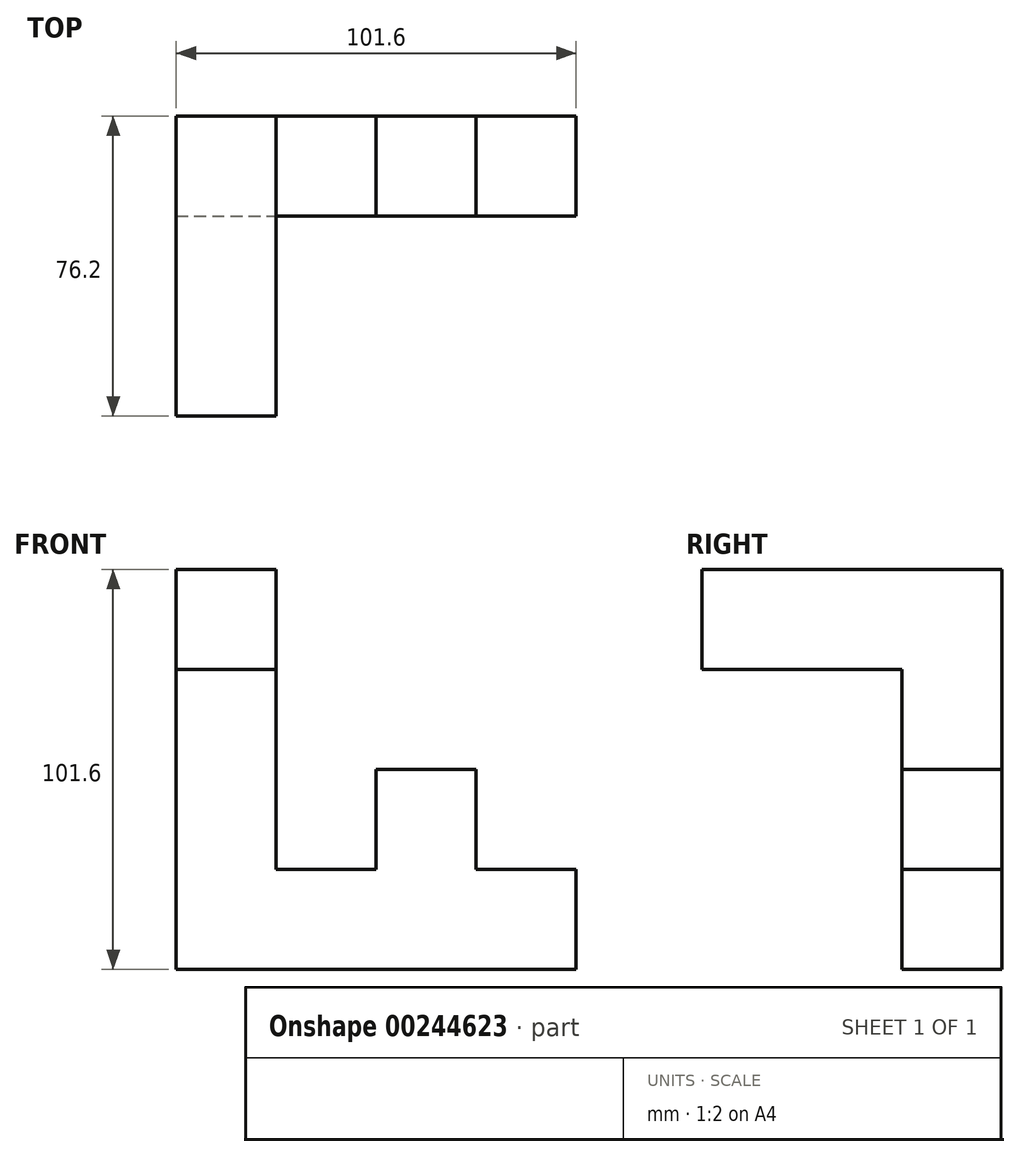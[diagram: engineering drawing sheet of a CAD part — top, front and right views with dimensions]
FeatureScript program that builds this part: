
annotation { "Feature Type Name" : "Feature", "Feature Type Description" : "" }
export const myFeature = defineFeature(function(context is Context, id is Id, definition is map)
    precondition{}
    {
        {
            var Q0;
            Q0=qCreatedBy(makeId("Top.planeOp"),FACE);
            var sketch = newSketch(context, id + "F0", { "sketchPlane" : qUnion([Q0])});
            skLineSegment(sketch, "E0.bottom", {"start": v(0, 0) * mm, "end": v(101.6, 0) * mm});
            skLineSegment(sketch, "E0.top", {"start": v(0, 25.4) * mm, "end": v(101.6, 25.4) * mm});
            skLineSegment(sketch, "E0.left", {"start": v(0, 0) * mm, "end": v(0, 25.4) * mm});
            skLineSegment(sketch, "E0.right", {"start": v(101.6, 0) * mm, "end": v(101.6, 25.4) * mm});
            skLineSegment(sketch, "E1", {"start": v(25.4, 25.4) * mm, "end": v(25.4, 0) * mm});
            skLineSegment(sketch, "E2", {"start": v(50.8, 25.4) * mm, "end": v(50.8, 0) * mm});
            skLineSegment(sketch, "E3", {"start": v(76.2, 25.4) * mm, "end": v(76.2, 0) * mm});
            skSolve(sketch);
        }
        {
            var Q0;
            {var subQ2=sQuery(id+"F0.wireOp",EDGE,"E1");Q0=makeQuery(id+"F0.imprint","IMPRINT",FACE,{"disambiguationData":[TD([[makeQuery(id+"F0.imprint","IMPRINT",EDGE,{"derivedFrom":subQ2}),1.0]])]});}
            var Q1;
            {var subQ2=sQuery(id+"F0.wireOp",EDGE,"E0.right");Q1=makeQuery(id+"F0.imprint","IMPRINT",FACE,{"disambiguationData":[TD([[makeQuery(id+"F0.imprint","IMPRINT",EDGE,{"derivedFrom":subQ2}),1.0]])]});}
            extrude(context, id + "F1", {"entities" : qUnion([Q0, Q1]), "depth" : 25.4 * mm, "offsetDistance" : 25.4 * mm});
        }
        {
            var Q0;
            {var subQ2=sQuery(id+"F0.wireOp",EDGE,"E2");Q0=makeQuery(id+"F0.imprint","IMPRINT",FACE,{"disambiguationData":[TD([[makeQuery(id+"F0.imprint","IMPRINT",EDGE,{"derivedFrom":subQ2}),1.0]])]});}
            extrude(context, id + "F2", {"entities" : qUnion([Q0]), "operationType" : NewBodyOperationType.ADD, "depth" : 50.8 * mm, "offsetDistance" : 25.4 * mm});
        }
        {
            var Q0;
            {var subQ0=sQuery(id+"F0.wireOp",EDGE,"E0.left");Q0=makeQuery(id+"F0.imprint","IMPRINT",FACE,{"disambiguationData":[TD([[makeQuery(id+"F0.imprint","IMPRINT",EDGE,{"derivedFrom":subQ0}),-1.0]])]});}
            extrude(context, id + "F3", {"entities" : qUnion([Q0]), "operationType" : NewBodyOperationType.ADD, "depth" : 101.6 * mm, "offsetDistance" : 25.4 * mm});
        }
        {
            var Q0;
            {var subQ0=sQuery(id+"F0.wireOp",EDGE,"E0.bottom");Q0=makeQuery(id+"F3.boolean.opBoolean","MERGE",FACE,{"derivedFrom":[makeQuery(id+"F2.boolean.opBoolean","MERGE",FACE,{"derivedFrom":[makeQuery(id+"F1.opExtrude","SWEPT_FACE",FACE,{"disambiguationData":[OSD([subQ0]),TDD([makeQuery(id+"F0.imprint","IMPRINT",EDGE,{"disambiguationData":[TD([[makeQuery(id+"F0.imprint","INTERSECT",VERTEX,{"derivedFrom":[subQ0,sQuery(id+"F0.wireOp",EDGE,"E3")]}),-1.0]])],"derivedFrom":subQ0})])]}),makeQuery(id+"F1.opExtrude","SWEPT_FACE",FACE,{"disambiguationData":[OSD([subQ0]),TDD([makeQuery(id+"F0.imprint","IMPRINT",EDGE,{"disambiguationData":[TD([[makeQuery(id+"F0.imprint","INTERSECT",VERTEX,{"derivedFrom":[subQ0,sQuery(id+"F0.wireOp",EDGE,"E2")]}),1.0]])],"derivedFrom":subQ0})])]}),makeQuery(id+"F2.opExtrude","SWEPT_FACE",FACE,{"disambiguationData":[OSD([subQ0])]})]}),makeQuery(id+"F3.opExtrude","SWEPT_FACE",FACE,{"disambiguationData":[OSD([subQ0])]})]});}
            var sketch = newSketch(context, id + "F4", { "sketchPlane" : qUnion([Q0])});
            skLineSegment(sketch, "E4.bottom", {"start": v(0, 101.6) * mm, "end": v(25.4, 101.6) * mm});
            skLineSegment(sketch, "E4.top", {"start": v(0, 76.2) * mm, "end": v(25.4, 76.2) * mm});
            skLineSegment(sketch, "E4.left", {"start": v(0, 101.6) * mm, "end": v(0, 76.2) * mm});
            skLineSegment(sketch, "E4.right", {"start": v(25.4, 101.6) * mm, "end": v(25.4, 76.2) * mm});
            skSolve(sketch);
        }
        {
            var Q0;
            Q0 = qSketchRegion(id + "F4", true);
            extrude(context, id + "F5", {"entities" : qUnion([Q0]), "operationType" : NewBodyOperationType.ADD, "depth" : 50.8 * mm, "offsetDistance" : 25.4 * mm});
        }
    });
